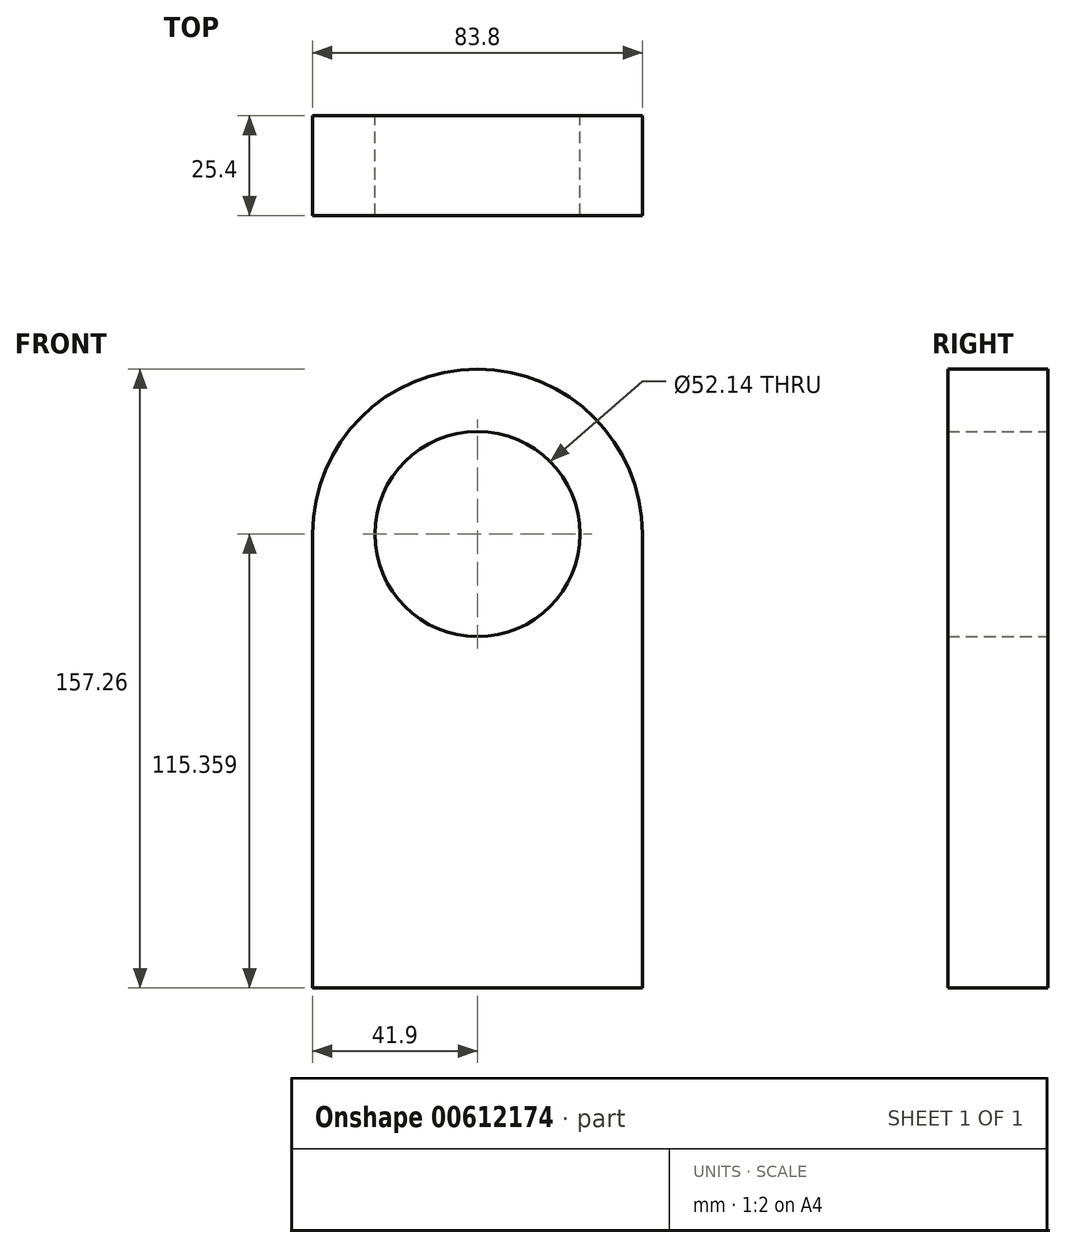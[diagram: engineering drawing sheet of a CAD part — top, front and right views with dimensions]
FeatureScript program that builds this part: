
annotation { "Feature Type Name" : "Feature", "Feature Type Description" : "" }
export const myFeature = defineFeature(function(context is Context, id is Id, definition is map)
    precondition{}
    {
        {
            var Q0;
            Q0=qCreatedBy(makeId("Front.planeOp"),FACE);
            var sketch = newSketch(context, id + "F0", { "sketchPlane" : qUnion([Q0])});
            skLineSegment(sketch, "E0.bottom", {"start": v(41.9, -57.68) * mm, "end": v(-41.9, -57.68) * mm});
            skLineSegment(sketch, "E0.left", {"start": v(41.9, -57.68) * mm, "end": v(41.9, 57.68) * mm});
            skLineSegment(sketch, "E0.right", {"start": v(-41.9, -57.68) * mm, "end": v(-41.9, 57.68) * mm});
            skPoint(sketch, "E0.middle", {"position": v(0, 0) * mm});
            skArc(sketch, "E1", {"start": v(-41.9, 57.68) * mm, "mid": v(0, 99.58) * mm, "end": v(41.9, 57.68) * mm});
            skCircle(sketch, "E2", {"center": v(0, 57.68) * mm, "radius": 26.07 * mm});
            skSolve(sketch);
        }
        {
            var Q0;
            Q0=makeQuery(id+"F0.imprint","IMPRINT",FACE,{"disambiguationData":[TD([[makeQuery(id+"F0.imprint","IMPRINT",EDGE,{"derivedFrom":sQuery(id+"F0.wireOp",EDGE,"E0.bottom")}),-1.0]])]});
            extrude(context, id + "F1", {"entities" : qUnion([Q0]), "depth" : 25.4 * mm, "offsetDistance" : 25.4 * mm});
        }
    });
